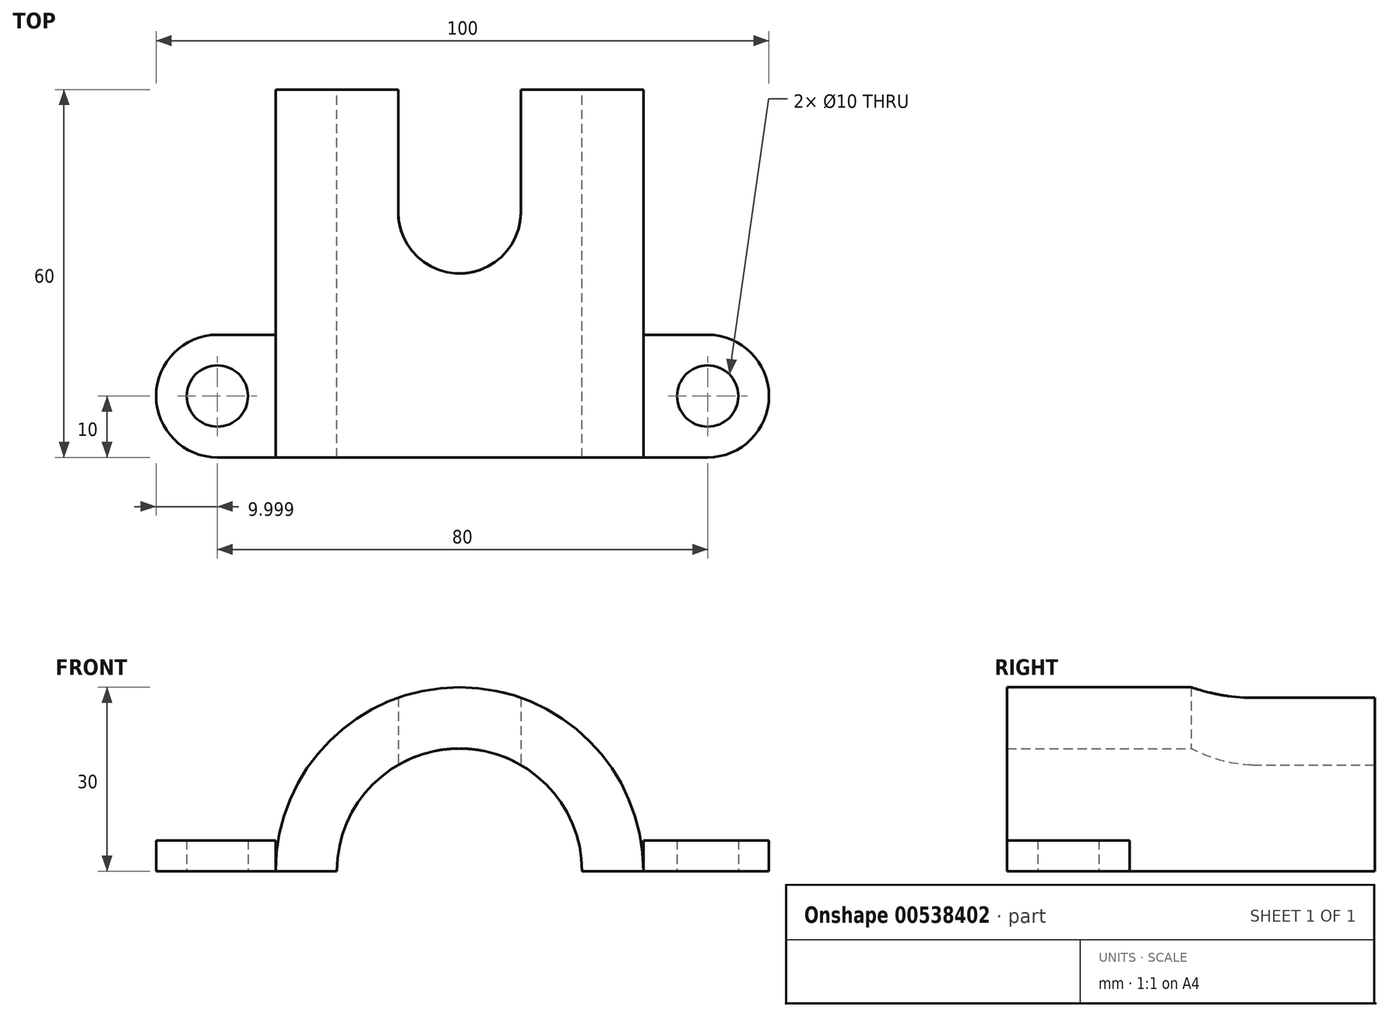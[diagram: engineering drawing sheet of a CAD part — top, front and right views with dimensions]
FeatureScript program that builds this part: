
annotation { "Feature Type Name" : "Feature", "Feature Type Description" : "" }
export const myFeature = defineFeature(function(context is Context, id is Id, definition is map)
    precondition{}
    {
        {
            var Q0;
            Q0=qCreatedBy(makeId("Front.planeOp"),FACE);
            var sketch = newSketch(context, id + "F0", { "sketchPlane" : qUnion([Q0])});
            skArc(sketch, "E0", {"start": v(30, 0) * mm, "mid": v(0, 30) * mm, "end": v(-30, 0) * mm});
            skLineSegment(sketch, "E1", {"start": v(30, 0) * mm, "end": v(20, 0) * mm});
            skArc(sketch, "E2", {"start": v(20, 0) * mm, "mid": v(0, 20) * mm, "end": v(-20, 0) * mm});
            skLineSegment(sketch, "E3", {"start": v(-30, 0) * mm, "end": v(-20, 0) * mm});
            skSolve(sketch);
        }
        {
            var Q0;
            Q0=makeQuery(id+"F0.imprint","IMPRINT",FACE,{"disambiguationData":[TD([[makeQuery(id+"F0.imprint","IMPRINT",EDGE,{"derivedFrom":sQuery(id+"F0.wireOp",EDGE,"E0")}),1.0]])]});
            extrude(context, id + "F1", {"entities" : qUnion([Q0]), "depth" : 60 * mm, "offsetDistance" : 25 * mm});
        }
        {
            var Q0;
            Q0=qCreatedBy(makeId("Top.planeOp"),FACE);
            var sketch = newSketch(context, id + "F2", { "sketchPlane" : qUnion([Q0])});
            skLineSegment(sketch, "E4.bottom", {"start": v(-10, -20) * mm, "end": v(10, -20) * mm});
            skLineSegment(sketch, "E4.top", {"start": v(-10, 20) * mm, "end": v(10, 20) * mm});
            skLineSegment(sketch, "E4.left", {"start": v(-10, -20) * mm, "end": v(-10, 20) * mm});
            skLineSegment(sketch, "E4.right", {"start": v(10, -20) * mm, "end": v(10, 20) * mm});
            skPoint(sketch, "E4.middle", {"position": v(0, 0) * mm});
            skArc(sketch, "E5", {"start": v(-10, -20) * mm, "mid": v(0, -30) * mm, "end": v(10, -20) * mm});
            skPoint(sketch, "E6", {"position": v(0, -30) * mm});
            skSolve(sketch);
        }
        {
            var Q0;
            Q0 = qSketchRegion(id + "F2", true);
            extrude(context, id + "F3", {"entities" : qUnion([Q0]), "operationType" : NewBodyOperationType.REMOVE, "endBound" : BoundingType.THROUGH_ALL, "depth" : 25 * mm, "offsetDistance" : 25 * mm});
        }
        {
            var Q0;
            Q0=qCreatedBy(makeId("Top.planeOp"),FACE);
            var sketch = newSketch(context, id + "F4", { "sketchPlane" : qUnion([Q0])});
            skLineSegment(sketch, "E7.bottom", {"start": v(-39.5, -40) * mm, "end": v(-30, -40) * mm});
            skLineSegment(sketch, "E7.top", {"start": v(-39.5, -60) * mm, "end": v(-30, -60) * mm});
            skLineSegment(sketch, "E7.left", {"start": v(-39.5, -40) * mm, "end": v(-39.5, -60) * mm});
            skLineSegment(sketch, "E7.right", {"start": v(-30, -40) * mm, "end": v(-30, -60) * mm});
            skPoint(sketch, "E7.middle", {"position": v(-34.75, -50) * mm});
            skLineSegment(sketch, "E8.bottom", {"start": v(40.5, -40) * mm, "end": v(30, -40) * mm});
            skLineSegment(sketch, "E8.top", {"start": v(40.5, -60) * mm, "end": v(30, -60) * mm});
            skLineSegment(sketch, "E8.left", {"start": v(40.5, -40) * mm, "end": v(40.5, -60) * mm});
            skLineSegment(sketch, "E8.right", {"start": v(30, -40) * mm, "end": v(30, -60) * mm});
            skPoint(sketch, "E8.middle", {"position": v(35.25, -50) * mm});
            skArc(sketch, "E9", {"start": v(40.5, -60) * mm, "mid": v(50.5, -50) * mm, "end": v(40.5, -40) * mm});
            skArc(sketch, "E10", {"start": v(-39.5, -40) * mm, "mid": v(-49.5, -50) * mm, "end": v(-39.5, -60) * mm});
            skCircle(sketch, "E11", {"center": v(40.5, -50) * mm, "radius": 5 * mm});
            skCircle(sketch, "E12", {"center": v(-39.5, -50) * mm, "radius": 5 * mm});
            skSolve(sketch);
        }
        {
            var Q0;
            Q0 = qSketchRegion(id + "F4", true);
            extrude(context, id + "F5", {"entities" : qUnion([Q0]), "depth" : 5 * mm, "offsetDistance" : 25 * mm});
        }
    });
